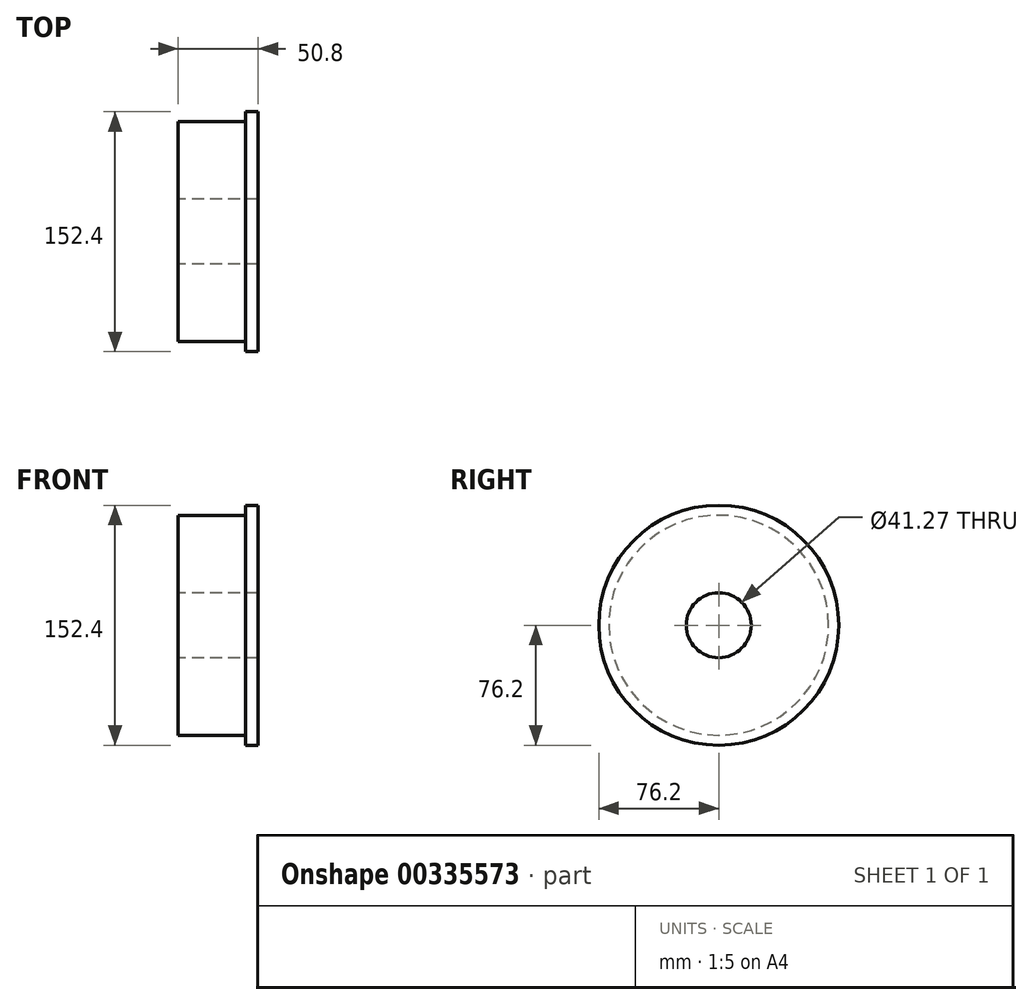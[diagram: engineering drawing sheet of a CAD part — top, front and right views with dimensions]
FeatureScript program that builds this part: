
annotation { "Feature Type Name" : "Feature", "Feature Type Description" : "" }
export const myFeature = defineFeature(function(context is Context, id is Id, definition is map)
    precondition{}
    {
        {
            var Q0;
            Q0=qCreatedBy(makeId("Right.planeOp"),FACE);
            var sketch = newSketch(context, id + "F0", { "sketchPlane" : qUnion([Q0])});
            skCircle(sketch, "E0", {"center": v(0, 0) * mm, "radius": 69.85 * mm});
            skCircle(sketch, "E1", {"center": v(0, 0) * mm, "radius": 20.64 * mm});
            skSolve(sketch);
        }
        {
            var Q0;
            Q0=qSketchRegion(id+"F0",true);
            extrude(context, id + "F1", {"entities" : qUnion([Q0]), "depth" : 42.93 * mm});
        }
        {
            var Q0;
            Q0=makeQuery(id+"F1.opExtrude","CAP_FACE",FACE,{"disambiguationData":[OSD([sQuery(id+"F0.wireOp",EDGE,"E0"),sQuery(id+"F0.wireOp",EDGE,"E1")])],"isStart":false});
            var sketch = newSketch(context, id + "F2", { "sketchPlane" : qUnion([Q0])});
            skCircle(sketch, "E2", {"center": v(0, 0) * mm, "radius": 76.2 * mm});
            skCircle(sketch, "E3.0", {"center": v(0, 0) * mm, "radius": 20.64 * mm});
            skSolve(sketch);
        }
        {
            var Q0;
            Q0=qSketchRegion(id+"F2",true);
            extrude(context, id + "F3", {"entities" : qUnion([Q0]), "operationType" : NewBodyOperationType.ADD, "depth" : 7.87 * mm});
        }
    });
